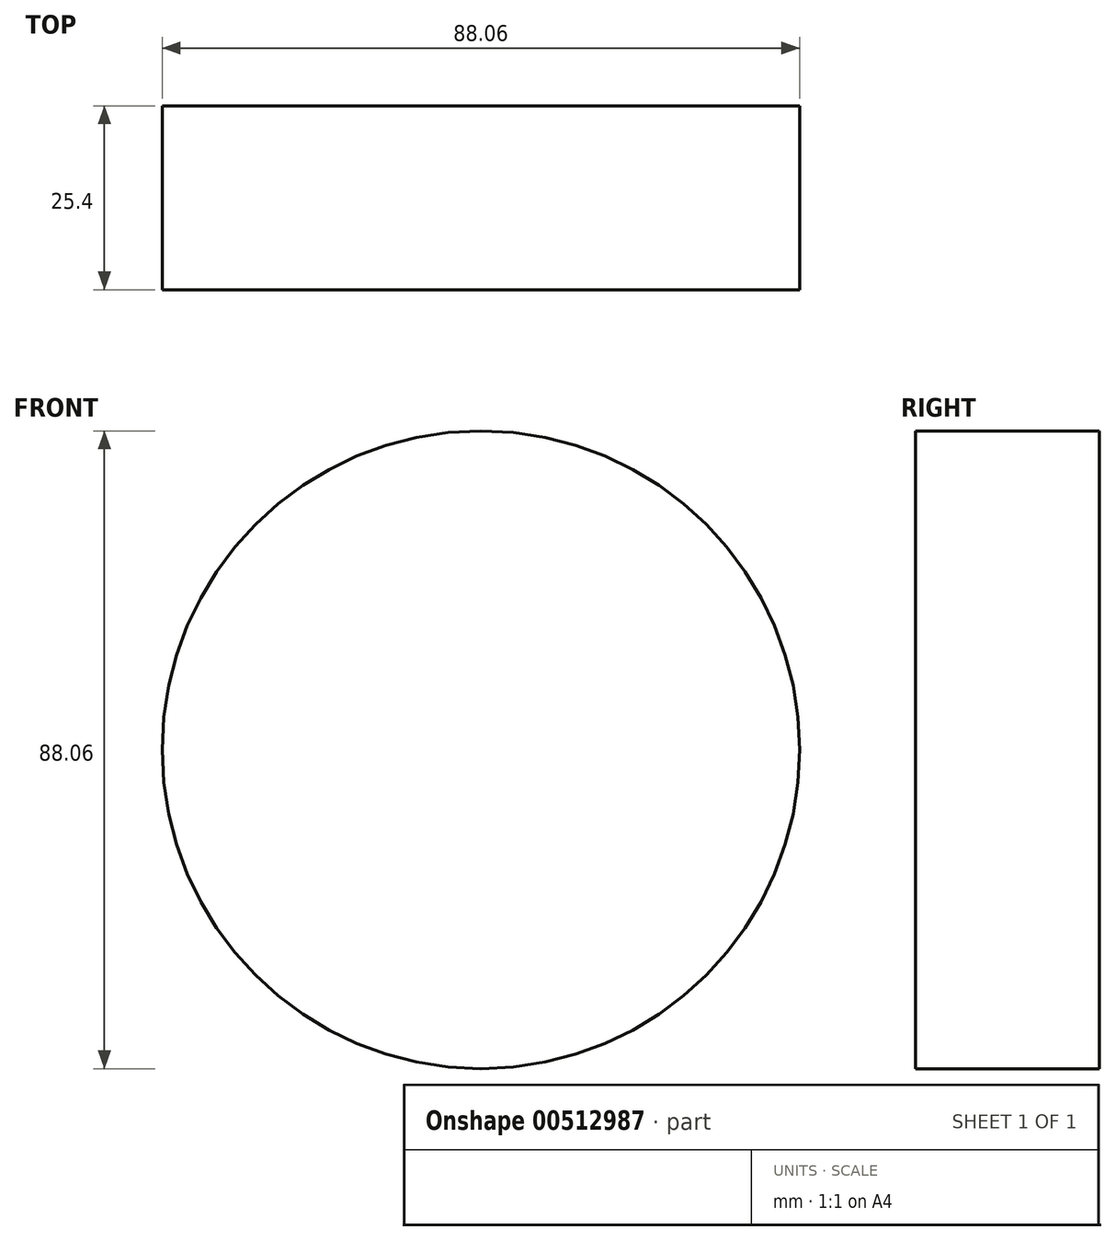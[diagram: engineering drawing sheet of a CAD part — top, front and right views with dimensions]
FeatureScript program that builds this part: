
annotation { "Feature Type Name" : "Feature", "Feature Type Description" : "" }
export const myFeature = defineFeature(function(context is Context, id is Id, definition is map)
    precondition{}
    {
        {
            var Q0;
            Q0=qCreatedBy(makeId("Front.planeOp"),FACE);
            var sketch = newSketch(context, id + "F0", { "sketchPlane" : qUnion([Q0])});
            skCircle(sketch, "E0", {"center": v(0, 0) * mm, "radius": 44.03 * mm});
            skSolve(sketch);
        }
        {
            var Q0;
            Q0=makeQuery(id+"F0.imprint","IMPRINT",FACE,{"disambiguationData":[TD([[makeQuery(id+"F0.imprint","IMPRINT",EDGE,{"derivedFrom":sQuery(id+"F0.wireOp",EDGE,"E0")}),1.0]])]});
            extrude(context, id + "F1", {"entities" : qUnion([Q0]), "depth" : 25.4 * mm});
        }
    });
